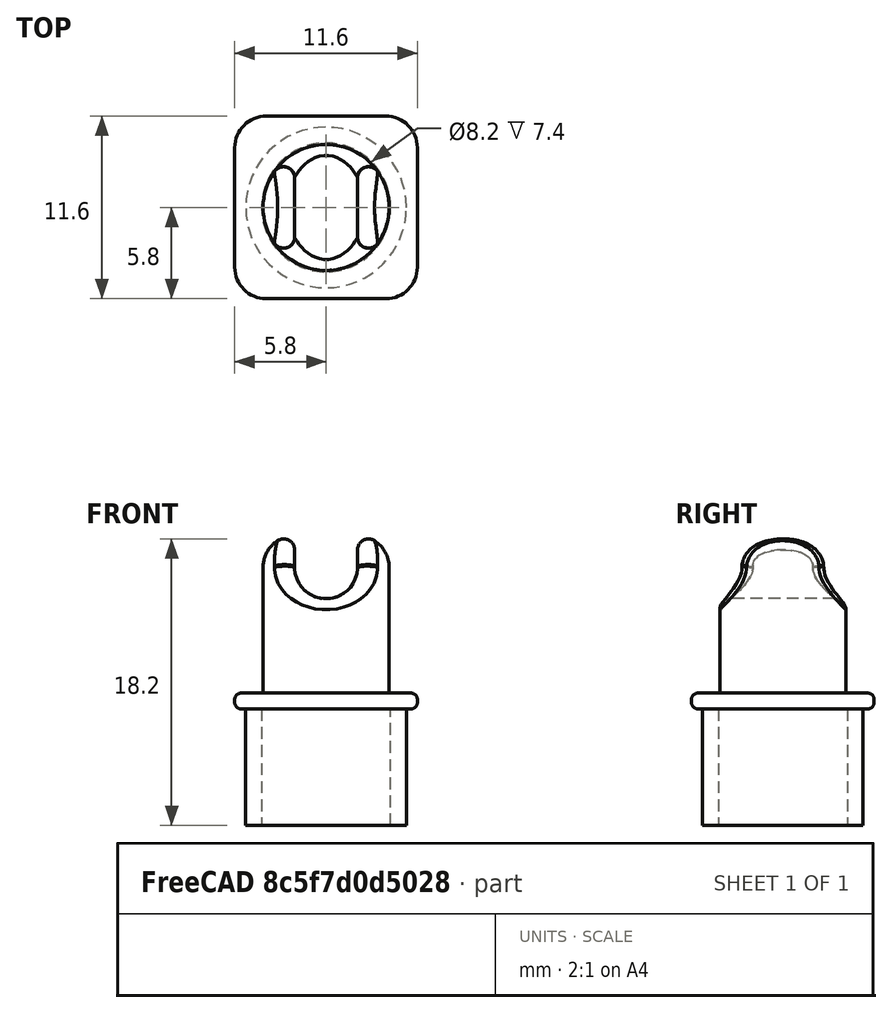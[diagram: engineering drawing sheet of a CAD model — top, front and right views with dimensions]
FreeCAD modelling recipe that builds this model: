
FCSTD DOCUMENT  (FreeCAD 0.20R28671 (Git))
Label: tapa pot linear
License: All rights reserved
LicenseURL: http://en.wikipedia.org/wiki/All_rights_reserved
objects: TechDraw::DrawViewDimension×13, Sketcher::SketchObject×5, PartDesign::Fillet×4, PartDesign::Pad×3, PartDesign::Pocket×2, TechDraw::DrawProjGroupItem×2, PartDesign::Body×1, TechDraw::DrawSVGTemplate×1, Part::Refine×1, TechDraw::DrawProjGroup×1, TechDraw::DrawViewSection×1, TechDraw::DrawViewAnnotation×1, TechDraw::DrawPage×1
note: 25 computed .brp shape members not serialized (recipe doc carries the construction recipe); baked Part::Feature solids carry a one-line shape summary decoded from their .brp

FEATURE [Sketcher::SketchObject] Sketch
  FullyConstrained = true
  MapMode = 5
  Support = -> [XY_Plane]
  sketch-geometry (4):
    g0: Circle CenterX=0 CenterY=0 CenterZ=0 NormalX=0 NormalY=0 NormalZ=1 AngleXU=0 Radius=5.1
    g1: Circle CenterX=0 CenterY=0 CenterZ=0 NormalX=0 NormalY=0 NormalZ=1 AngleXU=0 Radius=4.1
    g2: GeomPoint X=0 Y=4.1 Z=0
    g3: GeomPoint X=0 Y=5.1 Z=0
  constraints (8):
    c: Coincident(g0,g-1)
    c: Diameter(g0) = 10.2
    c: Coincident(g1,g0)
    c: PointOnObject(g2,g1)
    c: PointOnObject(g3,g0)
    c: Vertical(g2,g3)
    c: Vertical(g2,g0)
    c: DistanceY(g2,g3) = 1
FEATURE [PartDesign::Pad] Pad
  Direction = (1,1,1)
  Length = 12.4
  Length2 = 100
  Profile = -> Sketch
  Type = 0
FEATURE [Sketcher::SketchObject] Sketch001
  FullyConstrained = true
  MapMode = 5
  Placement = pos=(0,0,12.4) rot=(0,0,1;0rad)
  Support = -> [Pad]
  sketch-geometry (6):
    g0: LineSegment StartX=-5.8 StartY=5.8 StartZ=0 EndX=5.8 EndY=5.8 EndZ=0
    g1: LineSegment StartX=5.8 StartY=5.8 StartZ=0 EndX=5.8 EndY=-5.8 EndZ=0
    g2: LineSegment StartX=5.8 StartY=-5.8 StartZ=0 EndX=-5.8 EndY=-5.8 EndZ=0
    g3: LineSegment StartX=-5.8 StartY=-5.8 StartZ=0 EndX=-5.8 EndY=5.8 EndZ=0
    g4: LineSegment StartX=-5.8 StartY=5.8 StartZ=0 EndX=0 EndY=9e-16 EndZ=0
    g5: LineSegment StartX=0 StartY=0 StartZ=0 EndX=5.8 EndY=-5.8 EndZ=0
  constraints (16):
    c: Coincident(g0,g1)
    c: Coincident(g1,g2)
    c: Coincident(g2,g3)
    c: Coincident(g3,g0)
    c: Horizontal(g0)
    c: Horizontal(g2)
    c: Vertical(g1)
    c: Vertical(g3)
    c: Coincident(g4,g0)
    c: Coincident(g4,g-1)
    c: Coincident(g5,g-1)
    c: Coincident(g5,g1)
    c: Equal(g5,g4)
    c: Equal(g1,g2)
    c: DistanceX(g0,g0) = 11.6
    c: Parallel(g5,g4)
FEATURE [PartDesign::Pad] Pad001
  BaseFeature = -> Pad
  Direction = (1,1,1)
  Length = 1
  Length2 = 100
  Profile = -> Sketch001
  Type = 0
FEATURE [PartDesign::Fillet] Fillet
  Base = -> Pad001 [Edge5,Edge8,Edge2,Edge1]
  BaseFeature = -> Pad001
  Radius = 2
  SupportTransform = false
  UseAllEdges = false
FEATURE [PartDesign::Fillet] Fillet001
  Base = -> Fillet [Edge7,Edge17]
  BaseFeature = -> Fillet
  Radius = 0.4
  SupportTransform = false
  UseAllEdges = false
FEATURE [Sketcher::SketchObject] Sketch002
  FullyConstrained = true
  MapMode = 5
  Placement = pos=(0,0,13.4) rot=(0,0,1;0rad)
  Support = -> [Fillet001]
  sketch-geometry (1):
    g0: Circle CenterX=0 CenterY=0 CenterZ=0 NormalX=0 NormalY=0 NormalZ=1 AngleXU=0 Radius=4
  constraints (2):
    c: Coincident(g0,g-1)
    c: Radius(g0) = 4
FEATURE [PartDesign::Pad] Pad002
  BaseFeature = -> Fillet001
  Direction = (1,1,1)
  Length = 10
  Length2 = 100
  Profile = -> Sketch002
  Type = 0
FEATURE [PartDesign::Fillet] Fillet002
  Base = -> Pad002 [Edge61]
  BaseFeature = -> Pad002
  Radius = 2
  SupportTransform = false
  UseAllEdges = false
FEATURE [Sketcher::SketchObject] Sketch003
  ExternalGeometry = -> [Fillet002]
  FullyConstrained = true
  MapMode = 5
  Placement = pos=(0,0,0) rot=(1,0,0;1.5708rad)
  Support = -> [XZ_Plane]
  sketch-geometry (8):
    g0: ArcOfCircle CenterX=0 CenterY=21.4 CenterZ=0 NormalX=0 NormalY=0 NormalZ=1 AngleXU=0 Radius=2 StartAngle=3.14159 EndAngle=6.28319
    g1: LineSegment StartX=-2 StartY=21.4 StartZ=0 EndX=-2 EndY=25.4 EndZ=0
    g2: LineSegment StartX=2 StartY=21.4 StartZ=0 EndX=2 EndY=25.4 EndZ=0
    g3: LineSegment StartX=-2 StartY=25.4 StartZ=0 EndX=2 EndY=25.4 EndZ=0
    g4: LineSegment StartX=-2 StartY=23.4 StartZ=0 EndX=0 EndY=23.4 EndZ=0
    g5: LineSegment StartX=2 StartY=23.4 StartZ=0 EndX=0 EndY=23.4 EndZ=0
    g6: LineSegment StartX=0 StartY=21.4 StartZ=0 EndX=2 EndY=21.4 EndZ=0
    g7: LineSegment StartX=0 StartY=23.4 StartZ=0 EndX=0 EndY=25.4 EndZ=0
  constraints (23):
    c: PointOnObject(g0,g-2)
    c: Coincident(g1,g0)
    c: Vertical(g1)
    c: Coincident(g2,g0)
    c: Vertical(g2)
    c: Coincident(g3,g1)
    c: Coincident(g3,g2)
    c: Tangent(g0,g2)
    c: Tangent(g1,g0)
    c: DistanceX(g1,g2) = 4
    c: Coincident(g4,g-3)
    c: Coincident(g5,g-3)
    c: Coincident(g5,g4)
    c: Vertical(g4,g0)
    c: Horizontal(g5)
    c: DistanceY(g0,g5) = 2
    c: Coincident(g6,g0)
    c: Coincident(g6,g0)
    c: Coincident(g7,g4)
    c: PointOnObject(g7,g3)
    c: Vertical(g7)
    c: Equal(g7,g6)
    c: Horizontal(g3)
FEATURE [PartDesign::Pocket] Pocket
  BaseFeature = -> Fillet002
  Direction = (0,1,2e-16)
  Length = 5
  Length2 = 100
  Midplane = true
  Profile = -> Sketch003
  Type = 1
FEATURE [PartDesign::Fillet] Fillet003
  Base = -> Pocket [Edge4]
  BaseFeature = -> Pocket
  Radius = 0.7
  SupportTransform = false
  UseAllEdges = false
FEATURE [Sketcher::SketchObject] Sketch004
  ExternalGeometry = -> [Fillet003]
  FullyConstrained = true
  MapMode = 5
  Placement = pos=(0,0,0) rot=(1,0,0;1.5708rad)
  Support = -> [XZ_Plane]
  sketch-geometry (6):
    g0: LineSegment StartX=-5.8 StartY=0 StartZ=0 EndX=5.8 EndY=0 EndZ=0
    g1: LineSegment StartX=5.8 StartY=0 StartZ=0 EndX=5.8 EndY=5 EndZ=0
    g2: LineSegment StartX=5.8 StartY=5 StartZ=0 EndX=-5.8 EndY=5 EndZ=0
    g3: LineSegment StartX=-5.8 StartY=5 StartZ=0 EndX=-5.8 EndY=0 EndZ=0
    g4: LineSegment StartX=0 StartY=0 StartZ=0 EndX=-5.8 EndY=0 EndZ=0
    g5: LineSegment StartX=0 StartY=0 StartZ=0 EndX=5.8 EndY=0 EndZ=0
  constraints (16):
    c: Coincident(g0,g1)
    c: Coincident(g1,g2)
    c: Coincident(g2,g3)
    c: Coincident(g3,g0)
    c: Horizontal(g0)
    c: Horizontal(g2)
    c: Vertical(g1)
    c: Vertical(g3)
    c: DistanceY(g0,g1) = 5
    c: Coincident(g4,g-1)
    c: Coincident(g4,g0)
    c: Coincident(g5,g4)
    c: Coincident(g5,g0)
    c: Equal(g5,g4)
    c: Horizontal(g5)
    c: Vertical(g-3,g2)
FEATURE [PartDesign::Pocket] Pocket001
  BaseFeature = -> Fillet003
  Direction = (0,1,2e-16)
  Length = 5
  Length2 = 5
  Midplane = true
  Profile = -> Sketch004
  ReferenceAxis = -> Sketch004 [N_Axis]
  Type = 1
FEATURE [PartDesign::Body] Body
  Group = -> [Sketch,Pad,Sketch001,Pad001,Fillet,Fillet001,Sketch002,Pad002,Fillet002,Sketch003,Pocket,Fillet003,Sketch004,Pocket001]
  Origin = -> Origin
  Tip = -> Pocket001
FEATURE [TechDraw::DrawSVGTemplate] Template
  EditableTexts = AUTHOR_NAME=Daniel García García; DATE=15-04-2022; DN=13; DOCUMENT_TYPE=Plano de Pieza; PN=20; REVISION=1; SCALE=2:1; SHEET=13/15; SIZE=A4; TITLELINE-1=Tapa del potenciómetro lineal
  Height = 210
  Orientation = 1
  Width = 297
FEATURE [Part::Refine] Pocket001001
  Source = -> Pocket001
FEATURE [TechDraw::DrawProjGroupItem] ProjItem  label="Front"
  CoarseView = false
  Direction = (0,1,0)
  Focus = 100
  HardHidden = false
  IsoCount = 0
  IsoHidden = false
  IsoVisible = false
  LockPosition = true
  Perspective = false
  Rotation = 0
  RotationVector = (-1,0,0)
  Scale = 2
  ScaleType = 2
  SeamHidden = false
  SeamVisible = true
  SmoothHidden = false
  SmoothVisible = true
  Source = -> [Pocket001001]
  Type = 0
  X = 0
  XDirection = (-1,0,0)
  Y = 0
FEATURE [TechDraw::DrawProjGroupItem] ProjItem002  label="Top"
  CoarseView = false
  Direction = (0,0,1)
  Focus = 100
  HardHidden = false
  IsoCount = 0
  IsoHidden = false
  IsoVisible = false
  LockPosition = true
  Perspective = false
  Rotation = 0
  RotationVector = (1,0,0)
  ScaleType = 2
  SeamHidden = false
  SeamVisible = true
  SmoothHidden = false
  SmoothVisible = true
  Source = -> [Pocket001001]
  Type = 4
  X = 0
  XDirection = (-1,0,0)
  Y = -64.511
FEATURE [TechDraw::DrawProjGroup] ProjGroup
  Anchor = -> ProjItem
  AutoDistribute = true
  LockPosition = true
  ProjectionType = 0
  Rotation = 0
  Scale = 2
  ScaleType = 2
  Source = -> [Pocket001001]
  Views = -> [ProjItem,ProjItem002]
  X = 209.941
  Y = 149.407
  spacingX = 15
  spacingY = 15
FEATURE [TechDraw::DrawViewSection] SectionView  label="Section A - A"
  BaseView = -> ProjItem
  Caption = Sección A-A'
  CoarseView = false
  CutSurfaceDisplay = 2
  Direction = (-1,0,0)
  FileGeomPattern = <path>
  FileHatchPattern = <path>
  Focus = 100
  FuseBeforeCut = false
  HardHidden = false
  HatchScale = 1
  IsoCount = 0
  IsoHidden = false
  IsoVisible = false
  LockPosition = true
  NameGeomPattern = Diamond
  Perspective = false
  Rotation = 0
  Scale = 2
  ScaleType = 2
  SeamHidden = false
  SeamVisible = true
  SectionDirection = 1
  SectionNormal = (-1,0,0)
  SectionOrigin = (0,0,14.09)
  SectionSymbol = A
  SmoothHidden = false
  SmoothVisible = true
  Source = -> [Pocket001001]
  X = 100.643
  XDirection = (0,-1,0)
  Y = 149.1
FEATURE [TechDraw::DrawViewDimension] Dimension
  AngleOverride = false
  Arbitrary = false
  ArbitraryTolerances = false
  EqualTolerance = true
  ExtensionAngle = 0
  FormatSpec = ∅%.2w
  FormatSpecOverTolerance = %+.2w
  FormatSpecUnderTolerance = %+.2w
  Inverted = false
  LineAngle = 0
  LockPosition = false
  MeasureType = 1
  OverTolerance = 0
  References2D = -> [ProjItem]
  Rotation = 0
  ScaleType = 0
  TheoreticalExact = false
  Type = 0
  UnderTolerance = 0
  X = 26.7002
  Y = -11.1033
FEATURE [TechDraw::DrawViewDimension] Dimension001
  AngleOverride = false
  Arbitrary = false
  ArbitraryTolerances = false
  EqualTolerance = true
  ExtensionAngle = 0
  FormatSpec = ∅%.2w
  FormatSpecOverTolerance = %+.2w
  FormatSpecUnderTolerance = %+.2w
  Inverted = false
  LineAngle = 0
  LockPosition = false
  MeasureType = 1
  OverTolerance = 0
  References2D = -> [SectionView]
  Rotation = 0
  ScaleType = 0
  TheoreticalExact = false
  Type = 1
  UnderTolerance = 0
  X = 31.6026
  Y = -5.55432
FEATURE [TechDraw::DrawViewDimension] Dimension002
  AngleOverride = false
  Arbitrary = false
  ArbitraryTolerances = false
  EqualTolerance = true
  ExtensionAngle = 0
  FormatSpec = %.2w
  FormatSpecOverTolerance = %+.2w
  FormatSpecUnderTolerance = %+.2w
  Inverted = false
  LineAngle = 0
  LockPosition = false
  MeasureType = 1
  OverTolerance = 0
  References2D = -> [SectionView]
  Rotation = 0
  ScaleType = 0
  TheoreticalExact = false
  Type = 2
  UnderTolerance = 0
  X = -27.1909
  Y = 11.0965
FEATURE [TechDraw::DrawViewDimension] Dimension003
  AngleOverride = false
  Arbitrary = false
  ArbitraryTolerances = false
  EqualTolerance = true
  ExtensionAngle = 0
  FormatSpec = ∅%.2w
  FormatSpecOverTolerance = %+.2w
  FormatSpecUnderTolerance = %+.2w
  Inverted = false
  LineAngle = 0
  LockPosition = false
  MeasureType = 1
  OverTolerance = 0
  References2D = -> [ProjItem]
  Rotation = 0
  ScaleType = 0
  TheoreticalExact = false
  Type = 1
  UnderTolerance = 0
  X = -22.7979
  Y = 10.1532
FEATURE [TechDraw::DrawViewDimension] Dimension004
  AngleOverride = false
  Arbitrary = false
  ArbitraryTolerances = false
  EqualTolerance = true
  ExtensionAngle = 0
  FormatSpec = %.2w
  FormatSpecOverTolerance = %+.2w
  FormatSpecUnderTolerance = %+.2w
  Inverted = false
  LineAngle = 0
  LockPosition = false
  MeasureType = 1
  OverTolerance = 0
  References2D = -> [SectionView]
  Rotation = 0
  ScaleType = 0
  TheoreticalExact = false
  Type = 2
  UnderTolerance = 0
  X = -20.9082
  Y = -8.42004
FEATURE [TechDraw::DrawViewDimension] Dimension005
  AngleOverride = false
  Arbitrary = false
  ArbitraryTolerances = false
  EqualTolerance = true
  ExtensionAngle = 0
  FormatSpec = %.2w
  FormatSpecOverTolerance = %+.2w
  FormatSpecUnderTolerance = %+.2w
  Inverted = false
  LineAngle = 0
  LockPosition = false
  MeasureType = 1
  OverTolerance = 0
  References2D = -> [ProjItem]
  Rotation = 0
  ScaleType = 0
  TheoreticalExact = false
  Type = 2
  UnderTolerance = 0
  X = -24.1857
  Y = -0.16548
FEATURE [TechDraw::DrawViewDimension] Dimension006
  AngleOverride = false
  Arbitrary = false
  ArbitraryTolerances = false
  EqualTolerance = true
  ExtensionAngle = 0
  FormatSpec = R%.2w
  FormatSpecOverTolerance = %+.2w
  FormatSpecUnderTolerance = %+.2w
  Inverted = false
  LineAngle = 0
  LockPosition = false
  MeasureType = 1
  OverTolerance = 0
  References2D = -> [ProjItem]
  Rotation = 0
  ScaleType = 0
  TheoreticalExact = false
  Type = 4
  UnderTolerance = 0
  X = 26.2447
  Y = -4.54235
FEATURE [TechDraw::DrawViewDimension] Dimension007
  AngleOverride = false
  Arbitrary = false
  ArbitraryTolerances = false
  EqualTolerance = true
  ExtensionAngle = 0
  FormatSpec = R%.2w
  FormatSpecOverTolerance = %+.2w
  FormatSpecUnderTolerance = %+.2w
  Inverted = false
  LineAngle = 0
  LockPosition = false
  MeasureType = 1
  OverTolerance = 0
  References2D = -> [ProjItem]
  Rotation = 0
  ScaleType = 0
  TheoreticalExact = false
  Type = 4
  UnderTolerance = 0
  X = -20.6819
  Y = 26.7869
FEATURE [TechDraw::DrawViewDimension] Dimension008
  AngleOverride = false
  Arbitrary = false
  ArbitraryTolerances = false
  EqualTolerance = true
  ExtensionAngle = 0
  FormatSpec = R%.2w
  FormatSpecOverTolerance = %+.2w
  FormatSpecUnderTolerance = %+.2w
  Inverted = false
  LineAngle = 0
  LockPosition = false
  MeasureType = 1
  OverTolerance = 0
  References2D = -> [ProjItem]
  Rotation = 0
  ScaleType = 0
  TheoreticalExact = false
  Type = 4
  UnderTolerance = 0
  X = 17.6551
  Y = 16.5238
FEATURE [TechDraw::DrawViewDimension] Dimension009
  AngleOverride = false
  Arbitrary = false
  ArbitraryTolerances = false
  EqualTolerance = true
  ExtensionAngle = 0
  FormatSpec = R%.2w
  FormatSpecOverTolerance = %+.2w
  FormatSpecUnderTolerance = %+.2w
  Inverted = false
  LineAngle = 0
  LockPosition = false
  MeasureType = 1
  OverTolerance = 0
  References2D = -> [ProjItem]
  Rotation = 0
  ScaleType = 0
  TheoreticalExact = false
  Type = 4
  UnderTolerance = 0
  X = 17.941
  Y = 27.7836
FEATURE [TechDraw::DrawViewDimension] Dimension010
  AngleOverride = false
  Arbitrary = false
  ArbitraryTolerances = false
  EqualTolerance = true
  ExtensionAngle = 0
  FormatSpec = %.2w
  FormatSpecOverTolerance = %+.2w
  FormatSpecUnderTolerance = %+.2w
  Inverted = false
  LineAngle = 0
  LockPosition = false
  MeasureType = 1
  OverTolerance = 0
  References2D = -> [ProjItem]
  Rotation = 0
  ScaleType = 0
  TheoreticalExact = false
  Type = 2
  UnderTolerance = 0
  X = 23.4602
  Y = 6.79677
FEATURE [TechDraw::DrawViewDimension] Dimension011
  AngleOverride = false
  Arbitrary = false
  ArbitraryTolerances = false
  EqualTolerance = true
  ExtensionAngle = 0
  FormatSpec = ☐%.2w
  FormatSpecOverTolerance = %+.2w
  FormatSpecUnderTolerance = %+.2w
  Inverted = false
  LineAngle = 0
  LockPosition = false
  MeasureType = 1
  OverTolerance = 0
  References2D = -> [ProjItem002]
  Rotation = 0
  ScaleType = 0
  TheoreticalExact = false
  Type = 2
  UnderTolerance = 0
  X = -25.1151
  Y = 2.1588
FEATURE [TechDraw::DrawViewDimension] Dimension012
  AngleOverride = false
  Arbitrary = false
  ArbitraryTolerances = false
  EqualTolerance = true
  ExtensionAngle = 0
  FormatSpec = R%.2w
  FormatSpecOverTolerance = %+.2w
  FormatSpecUnderTolerance = %+.2w
  Inverted = false
  LineAngle = 0
  LockPosition = false
  MeasureType = 1
  OverTolerance = 0
  References2D = -> [ProjItem002]
  Rotation = 0
  ScaleType = 0
  TheoreticalExact = false
  Type = 4
  UnderTolerance = 0
  X = 22.0645
  Y = 22.1782
FEATURE [TechDraw::DrawViewAnnotation] Annotation
  Font = osifont
  LineSpace = 80
  LockPosition = true
  MaxWidth = -1
  Rotation = 0
  ScaleType = 0
  Text = '
  TextSize = 5
  TextStyle = 0
  X = 212.075
  Y = 111.847
FEATURE [TechDraw::DrawPage] Page  label="Tapa del potenciómetro"
  KeepUpdated = true
  NextBalloonIndex = 1
  ProjectionType = 0
  Template = -> Template
  Views = -> [ProjGroup,SectionView,Dimension,Dimension001,Dimension002,Dimension003,Dimension004,Dimension005,Dimension006,Dimension007,Dimension008,Dimension009,Dimension010,Dimension011,Dimension012,Annotation]
note: 2 file-system paths scrubbed to <path> (originals preserved in the JSON sidecar)
